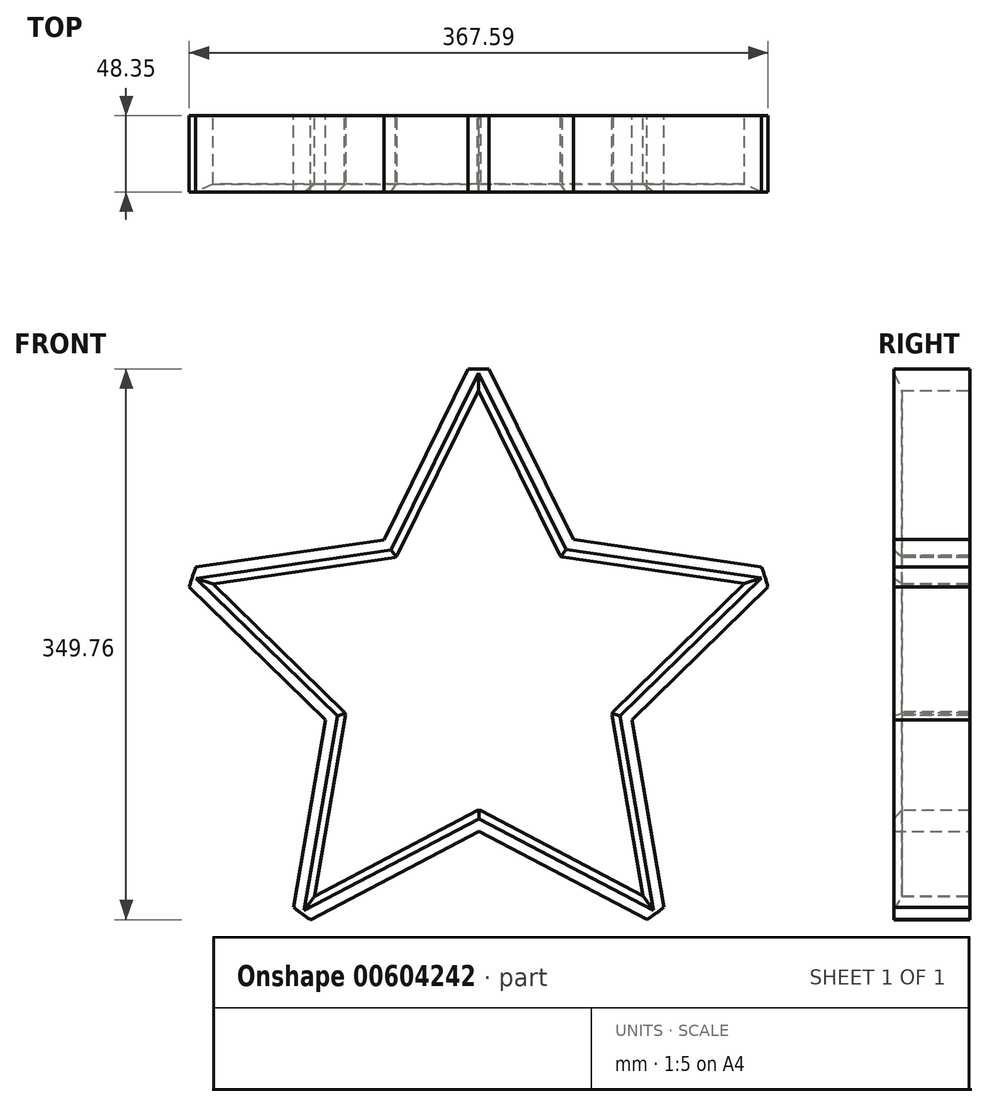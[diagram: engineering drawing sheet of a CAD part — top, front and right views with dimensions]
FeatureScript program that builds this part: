
annotation { "Feature Type Name" : "Feature", "Feature Type Description" : "" }
export const myFeature = defineFeature(function(context is Context, id is Id, definition is map)
    precondition{}
    {
        {
            var Q0;
            Q0=qCreatedBy(makeId("Front.planeOp"),FACE);
            var sketch = newSketch(context, id + "F0", { "sketchPlane" : qUnion([Q0])});
            skCircle(sketch, "E0", {"center": v(0, 0) * mm, "radius": 191.2 * mm});
            skCircle(sketch, "E1.cCircle", {"center": v(0, 0) * mm, "radius": 191.2 * mm, "construction": true});
            skLineSegment(sketch, "E2.0", {"start": v(0, -95.6) * mm, "end": v(-90.92, -29.54) * mm});
            skLineSegment(sketch, "E2.1", {"start": v(-90.92, -29.54) * mm, "end": v(-56.2, 77.34) * mm});
            skLineSegment(sketch, "E2.2", {"start": v(-56.2, 77.34) * mm, "end": v(56.2, 77.34) * mm});
            skLineSegment(sketch, "E2.3", {"start": v(56.2, 77.34) * mm, "end": v(90.92, -29.54) * mm});
            skLineSegment(sketch, "E2.4", {"start": v(90.92, -29.54) * mm, "end": v(0, -95.6) * mm});
            skLineSegment(sketch, "E3", {"start": v(-181.84, 59.08) * mm, "end": v(-90.92, -29.54) * mm});
            skLineSegment(sketch, "E4", {"start": v(-90.92, -29.54) * mm, "end": v(-112.38, -154.68) * mm});
            skLineSegment(sketch, "E5", {"start": v(-112.38, -154.68) * mm, "end": v(0, -95.6) * mm});
            skLineSegment(sketch, "E6", {"start": v(0, -95.6) * mm, "end": v(112.38, -154.68) * mm});
            skLineSegment(sketch, "E7", {"start": v(112.38, -154.68) * mm, "end": v(90.92, -29.54) * mm});
            skLineSegment(sketch, "E8", {"start": v(90.92, -29.54) * mm, "end": v(181.84, 59.08) * mm});
            skLineSegment(sketch, "E9", {"start": v(181.84, 59.08) * mm, "end": v(56.2, 77.34) * mm});
            skLineSegment(sketch, "E10", {"start": v(56.2, 77.34) * mm, "end": v(0, 191.2) * mm});
            skLineSegment(sketch, "E11", {"start": v(0, 191.2) * mm, "end": v(-56.2, 77.34) * mm});
            skLineSegment(sketch, "E12", {"start": v(-56.2, 77.34) * mm, "end": v(-181.84, 59.08) * mm});
            skLineSegment(sketch, "E13", {"start": v(-183.81, 52.63) * mm, "end": v(-92.15, -36.72) * mm});
            skLineSegment(sketch, "E14", {"start": v(-179.68, 65.36) * mm, "end": v(-88.85, -23.18) * mm});
            skLineSegment(sketch, "E15", {"start": v(-183.81, 52.63) * mm, "end": v(-58.3, 70.87) * mm});
            skLineSegment(sketch, "E16", {"start": v(-179.68, 65.36) * mm, "end": v(-53.02, 83.76) * mm});
            skLineSegment(sketch, "E17.2.0", {"start": v(6.63, 191.08) * mm, "end": v(63.28, 76.31) * mm});
            skLineSegment(sketch, "E17.2.1", {"start": v(-6.75, 191.08) * mm, "end": v(49.38, 77.34) * mm});
            skLineSegment(sketch, "E17.2.2", {"start": v(6.63, 191.08) * mm, "end": v(-49.5, 77.34) * mm});
            skLineSegment(sketch, "E17.2.3", {"start": v(-6.75, 191.08) * mm, "end": v(-63.4, 76.3) * mm});
            skLineSegment(sketch, "E17.4.0", {"start": v(183.78, 52.74) * mm, "end": v(92.13, -36.6) * mm});
            skLineSegment(sketch, "E17.4.1", {"start": v(179.64, 65.47) * mm, "end": v(88.82, -23.07) * mm});
            skLineSegment(sketch, "E17.4.2", {"start": v(183.78, 52.74) * mm, "end": v(58.26, 70.98) * mm});
            skLineSegment(sketch, "E17.4.3", {"start": v(179.64, 65.47) * mm, "end": v(52.97, 83.87) * mm});
            skLineSegment(sketch, "E17.anchor1", {"start": v(0, 0) * mm, "end": v(-179.68, 65.36) * mm, "construction": true});
            skLineSegment(sketch, "E17.anchor2", {"start": v(0, 0) * mm, "end": v(183.78, 52.74) * mm, "construction": true});
            skLineSegment(sketch, "E18.1.0", {"start": v(117.78, -150.62) * mm, "end": v(96.14, -24.46) * mm});
            skLineSegment(sketch, "E18.1.1", {"start": v(106.95, -158.5) * mm, "end": v(85.5, -33.47) * mm});
            skLineSegment(sketch, "E18.1.2", {"start": v(117.78, -150.62) * mm, "end": v(5.5, -91.6) * mm});
            skLineSegment(sketch, "E18.1.3", {"start": v(106.95, -158.5) * mm, "end": v(-6.34, -98.93) * mm});
            skLineSegment(sketch, "E18.2.0", {"start": v(-106.85, -158.56) * mm, "end": v(6.45, -98.99) * mm});
            skLineSegment(sketch, "E18.2.1", {"start": v(-117.68, -150.7) * mm, "end": v(-5.41, -91.67) * mm});
            skLineSegment(sketch, "E18.2.2", {"start": v(-106.85, -158.56) * mm, "end": v(-85.41, -33.54) * mm});
            skLineSegment(sketch, "E18.2.3", {"start": v(-117.68, -150.7) * mm, "end": v(-96.05, -24.54) * mm});
            skLineSegment(sketch, "E18.anchor1", {"start": v(0, 0) * mm, "end": v(52.97, 83.87) * mm, "construction": true});
            skLineSegment(sketch, "E18.anchor2", {"start": v(0, 0) * mm, "end": v(6.45, -98.99) * mm, "construction": true});
            skLineSegment(sketch, "E19", {"start": v(-58.3, 70.87) * mm, "end": v(-52.12, 71.76) * mm});
            skLineSegment(sketch, "E20", {"start": v(-49.5, 77.34) * mm, "end": v(-52.26, 71.74) * mm});
            skLineSegment(sketch, "E21.1.0", {"start": v(58.26, 70.98) * mm, "end": v(52.08, 71.88) * mm});
            skLineSegment(sketch, "E21.1.1", {"start": v(49.38, 77.34) * mm, "end": v(52.15, 71.75) * mm});
            skLineSegment(sketch, "E21.2.0", {"start": v(85.5, -33.47) * mm, "end": v(84.45, -27.32) * mm});
            skLineSegment(sketch, "E21.2.1", {"start": v(88.82, -23.07) * mm, "end": v(84.35, -27.42) * mm});
            skLineSegment(sketch, "E21.3.0", {"start": v(-5.41, -91.67) * mm, "end": v(0.11, -88.76) * mm});
            skLineSegment(sketch, "E21.3.1", {"start": v(5.5, -91.6) * mm, "end": v(-0.01, -88.7) * mm});
            skLineSegment(sketch, "E21.4.0", {"start": v(-88.85, -23.18) * mm, "end": v(-84.38, -27.54) * mm});
            skLineSegment(sketch, "E21.4.1", {"start": v(-85.41, -33.54) * mm, "end": v(-84.36, -27.4) * mm});
            skLineSegment(sketch, "E21.anchor1", {"start": v(0, 0) * mm, "end": v(-52.26, 71.74) * mm, "construction": true});
            skLineSegment(sketch, "E21.anchor2", {"start": v(0, 0) * mm, "end": v(-84.38, -27.54) * mm, "construction": true});
            skSolve(sketch);
        }
        {
            var Q0;
            {var subQ0=sQuery(id+"F0.wireOp",EDGE,"E11");var subQ5=sQuery(id+"F0.wireOp",EDGE,"E17.2.1");var subQ6=makeQuery(id+"F0.imprint","INTERSECT",VERTEX,{"derivedFrom":[subQ0,subQ5]});Q0=makeQuery(id+"F0.imprint","IMPRINT",FACE,{"disambiguationData":[TD([[makeQuery(id+"F0.imprint","IMPRINT",EDGE,{"disambiguationData":[TD([[subQ6,-1.0]])],"derivedFrom":subQ5}),1.0]])]});}
            var Q1;
            {var subQ0=sQuery(id+"F0.wireOp",EDGE,"E10");var subQ3=sQuery(id+"F0.wireOp",EDGE,"E17.2.2");var subQ5=makeQuery(id+"F0.imprint","INTERSECT",VERTEX,{"derivedFrom":[subQ0,subQ3]});Q1=makeQuery(id+"F0.imprint","IMPRINT",FACE,{"disambiguationData":[TD([[makeQuery(id+"F0.imprint","IMPRINT",EDGE,{"disambiguationData":[TD([[subQ5,-1.0]])],"derivedFrom":subQ0}),-1.0]])]});}
            var Q2;
            {var subQ0=sQuery(id+"F0.wireOp",EDGE,"E11");var subQ3=sQuery(id+"F0.wireOp",EDGE,"E17.2.1");var subQ5=makeQuery(id+"F0.imprint","INTERSECT",VERTEX,{"derivedFrom":[subQ0,subQ3]});Q2=makeQuery(id+"F0.imprint","IMPRINT",FACE,{"disambiguationData":[TD([[makeQuery(id+"F0.imprint","IMPRINT",EDGE,{"disambiguationData":[TD([[subQ5,1.0]])],"derivedFrom":subQ0}),-1.0]])]});}
            var Q3;
            {var subQ0=sQuery(id+"F0.wireOp",EDGE,"E16");var subQ1=sQuery(id+"F0.wireOp",EDGE,"E11");var subQ2=makeQuery(id+"F0.imprint","INTERSECT",VERTEX,{"derivedFrom":[subQ1,subQ0]});Q3=makeQuery(id+"F0.imprint","IMPRINT",FACE,{"disambiguationData":[TD([[makeQuery(id+"F0.imprint","IMPRINT",EDGE,{"disambiguationData":[TD([[subQ2,1.0]])],"derivedFrom":subQ1}),-1.0]])]});}
            var Q4;
            {var subQ1=sQuery(id+"F0.wireOp",EDGE,"E11");var subQ5=makeQuery(id+"F0.imprint","INTERSECT",VERTEX,{"derivedFrom":[subQ1,sQuery(id+"F0.wireOp",EDGE,"E16")]});Q4=makeQuery(id+"F0.imprint","IMPRINT",FACE,{"disambiguationData":[TD([[makeQuery(id+"F0.imprint","IMPRINT",EDGE,{"disambiguationData":[TD([[subQ5,1.0]])],"derivedFrom":subQ1}),1.0]])]});}
            var Q5;
            {var subQ5=sQuery(id+"F0.wireOp",EDGE,"E10");var subQ6=makeQuery(id+"F0.imprint","INTERSECT",VERTEX,{"derivedFrom":[subQ5,sQuery(id+"F0.wireOp",EDGE,"E17.4.3")]});Q5=makeQuery(id+"F0.imprint","IMPRINT",FACE,{"disambiguationData":[TD([[makeQuery(id+"F0.imprint","IMPRINT",EDGE,{"disambiguationData":[TD([[subQ6,-1.0]])],"derivedFrom":subQ5}),1.0]])]});}
            var Q6;
            {var subQ0=sQuery(id+"F0.wireOp",EDGE,"E17.4.3");var subQ1=sQuery(id+"F0.wireOp",EDGE,"E10");var subQ2=makeQuery(id+"F0.imprint","INTERSECT",VERTEX,{"derivedFrom":[subQ1,subQ0]});Q6=makeQuery(id+"F0.imprint","IMPRINT",FACE,{"disambiguationData":[TD([[makeQuery(id+"F0.imprint","IMPRINT",EDGE,{"disambiguationData":[TD([[subQ2,-1.0]])],"derivedFrom":subQ1}),-1.0]])]});}
            var Q7;
            {var subQ5=sQuery(id+"F0.wireOp",EDGE,"E21.1.0");Q7=makeQuery(id+"F0.imprint","IMPRINT",FACE,{"disambiguationData":[TD([[makeQuery(id+"F0.imprint","IMPRINT",EDGE,{"derivedFrom":subQ5}),-1.0]])]});}
            var Q8;
            {var subQ1=sQuery(id+"F0.wireOp",EDGE,"E9");var subQ3=sQuery(id+"F0.wireOp",EDGE,"E17.2.0");var subQ4=makeQuery(id+"F0.imprint","INTERSECT",VERTEX,{"derivedFrom":[subQ1,subQ3]});Q8=makeQuery(id+"F0.imprint","IMPRINT",FACE,{"disambiguationData":[TD([[makeQuery(id+"F0.imprint","IMPRINT",EDGE,{"disambiguationData":[TD([[subQ4,1.0]])],"derivedFrom":subQ3}),-1.0]])]});}
            var Q9;
            {var subQ0=sQuery(id+"F0.wireOp",EDGE,"E17.2.0");var subQ1=sQuery(id+"F0.wireOp",EDGE,"E9");var subQ2=makeQuery(id+"F0.imprint","INTERSECT",VERTEX,{"derivedFrom":[subQ1,subQ0]});Q9=makeQuery(id+"F0.imprint","IMPRINT",FACE,{"disambiguationData":[TD([[makeQuery(id+"F0.imprint","IMPRINT",EDGE,{"disambiguationData":[TD([[subQ2,1.0]])],"derivedFrom":subQ1}),-1.0]])]});}
            var Q10;
            {var subQ1=sQuery(id+"F0.wireOp",EDGE,"E9");var subQ7=makeQuery(id+"F0.imprint","INTERSECT",VERTEX,{"derivedFrom":[subQ1,sQuery(id+"F0.wireOp",EDGE,"E17.2.0")]});Q10=makeQuery(id+"F0.imprint","IMPRINT",FACE,{"disambiguationData":[TD([[makeQuery(id+"F0.imprint","IMPRINT",EDGE,{"disambiguationData":[TD([[subQ7,1.0]])],"derivedFrom":subQ1}),1.0]])]});}
            var Q11;
            {var subQ5=sQuery(id+"F0.wireOp",EDGE,"E8");var subQ7=makeQuery(id+"F0.imprint","INTERSECT",VERTEX,{"derivedFrom":[subQ5,sQuery(id+"F0.wireOp",EDGE,"E18.1.0")]});Q11=makeQuery(id+"F0.imprint","IMPRINT",FACE,{"disambiguationData":[TD([[makeQuery(id+"F0.imprint","IMPRINT",EDGE,{"disambiguationData":[TD([[subQ7,-1.0]])],"derivedFrom":subQ5}),1.0]])]});}
            var Q12;
            {var subQ0=sQuery(id+"F0.wireOp",EDGE,"E18.1.0");var subQ1=sQuery(id+"F0.wireOp",EDGE,"E8");var subQ2=makeQuery(id+"F0.imprint","INTERSECT",VERTEX,{"derivedFrom":[subQ1,subQ0]});Q12=makeQuery(id+"F0.imprint","IMPRINT",FACE,{"disambiguationData":[TD([[makeQuery(id+"F0.imprint","IMPRINT",EDGE,{"disambiguationData":[TD([[subQ2,-1.0]])],"derivedFrom":subQ1}),-1.0]])]});}
            var Q13;
            {var subQ0=sQuery(id+"F0.wireOp",EDGE,"E9");var subQ5=sQuery(id+"F0.wireOp",EDGE,"E17.4.1");var subQ6=makeQuery(id+"F0.imprint","INTERSECT",VERTEX,{"derivedFrom":[subQ0,subQ5]});Q13=makeQuery(id+"F0.imprint","IMPRINT",FACE,{"disambiguationData":[TD([[makeQuery(id+"F0.imprint","IMPRINT",EDGE,{"disambiguationData":[TD([[subQ6,-1.0]])],"derivedFrom":subQ5}),1.0]])]});}
            var Q14;
            {var subQ0=sQuery(id+"F0.wireOp",EDGE,"E9");var subQ3=sQuery(id+"F0.wireOp",EDGE,"E17.4.1");var subQ5=makeQuery(id+"F0.imprint","INTERSECT",VERTEX,{"derivedFrom":[subQ0,subQ3]});Q14=makeQuery(id+"F0.imprint","IMPRINT",FACE,{"disambiguationData":[TD([[makeQuery(id+"F0.imprint","IMPRINT",EDGE,{"disambiguationData":[TD([[subQ5,1.0]])],"derivedFrom":subQ0}),-1.0]])]});}
            var Q15;
            {var subQ0=sQuery(id+"F0.wireOp",EDGE,"E8");var subQ3=sQuery(id+"F0.wireOp",EDGE,"E17.4.2");var subQ5=makeQuery(id+"F0.imprint","INTERSECT",VERTEX,{"derivedFrom":[subQ0,subQ3]});Q15=makeQuery(id+"F0.imprint","IMPRINT",FACE,{"disambiguationData":[TD([[makeQuery(id+"F0.imprint","IMPRINT",EDGE,{"disambiguationData":[TD([[subQ5,-1.0]])],"derivedFrom":subQ0}),-1.0]])]});}
            var Q16;
            {var subQ5=sQuery(id+"F0.wireOp",EDGE,"E21.2.0");Q16=makeQuery(id+"F0.imprint","IMPRINT",FACE,{"disambiguationData":[TD([[makeQuery(id+"F0.imprint","IMPRINT",EDGE,{"derivedFrom":subQ5}),-1.0]])]});}
            var Q17;
            {var subQ1=sQuery(id+"F0.wireOp",EDGE,"E7");var subQ3=sQuery(id+"F0.wireOp",EDGE,"E17.4.0");var subQ4=makeQuery(id+"F0.imprint","INTERSECT",VERTEX,{"derivedFrom":[subQ1,subQ3]});Q17=makeQuery(id+"F0.imprint","IMPRINT",FACE,{"disambiguationData":[TD([[makeQuery(id+"F0.imprint","IMPRINT",EDGE,{"disambiguationData":[TD([[subQ4,1.0]])],"derivedFrom":subQ3}),-1.0]])]});}
            var Q18;
            {var subQ5=sQuery(id+"F0.wireOp",EDGE,"E7");var subQ7=makeQuery(id+"F0.imprint","INTERSECT",VERTEX,{"derivedFrom":[subQ5,sQuery(id+"F0.wireOp",EDGE,"E17.4.0")]});Q18=makeQuery(id+"F0.imprint","IMPRINT",FACE,{"disambiguationData":[TD([[makeQuery(id+"F0.imprint","IMPRINT",EDGE,{"disambiguationData":[TD([[subQ7,1.0]])],"derivedFrom":subQ5}),1.0]])]});}
            var Q19;
            {var subQ0=sQuery(id+"F0.wireOp",EDGE,"E17.4.0");var subQ1=sQuery(id+"F0.wireOp",EDGE,"E7");var subQ2=makeQuery(id+"F0.imprint","INTERSECT",VERTEX,{"derivedFrom":[subQ1,subQ0]});Q19=makeQuery(id+"F0.imprint","IMPRINT",FACE,{"disambiguationData":[TD([[makeQuery(id+"F0.imprint","IMPRINT",EDGE,{"disambiguationData":[TD([[subQ2,1.0]])],"derivedFrom":subQ1}),-1.0]])]});}
            var Q20;
            {var subQ1=sQuery(id+"F0.wireOp",EDGE,"E6");var subQ3=sQuery(id+"F0.wireOp",EDGE,"E18.1.1");var subQ4=makeQuery(id+"F0.imprint","INTERSECT",VERTEX,{"derivedFrom":[subQ1,subQ3]});Q20=makeQuery(id+"F0.imprint","IMPRINT",FACE,{"disambiguationData":[TD([[makeQuery(id+"F0.imprint","IMPRINT",EDGE,{"disambiguationData":[TD([[subQ4,-1.0]])],"derivedFrom":subQ3}),-1.0]])]});}
            var Q21;
            {var subQ0=sQuery(id+"F0.wireOp",EDGE,"E7");var subQ3=sQuery(id+"F0.wireOp",EDGE,"E18.1.2");var subQ5=makeQuery(id+"F0.imprint","INTERSECT",VERTEX,{"derivedFrom":[subQ0,subQ3]});Q21=makeQuery(id+"F0.imprint","IMPRINT",FACE,{"disambiguationData":[TD([[makeQuery(id+"F0.imprint","IMPRINT",EDGE,{"disambiguationData":[TD([[subQ5,1.0]])],"derivedFrom":subQ0}),-1.0]])]});}
            var Q22;
            {var subQ0=sQuery(id+"F0.wireOp",EDGE,"E6");var subQ3=sQuery(id+"F0.wireOp",EDGE,"E18.1.1");var subQ5=makeQuery(id+"F0.imprint","INTERSECT",VERTEX,{"derivedFrom":[subQ0,subQ3]});Q22=makeQuery(id+"F0.imprint","IMPRINT",FACE,{"disambiguationData":[TD([[makeQuery(id+"F0.imprint","IMPRINT",EDGE,{"disambiguationData":[TD([[subQ5,-1.0]])],"derivedFrom":subQ0}),-1.0]])]});}
            var Q23;
            {var subQ0=sQuery(id+"F0.wireOp",EDGE,"E18.2.0");var subQ1=sQuery(id+"F0.wireOp",EDGE,"E6");var subQ2=makeQuery(id+"F0.imprint","INTERSECT",VERTEX,{"derivedFrom":[subQ1,subQ0]});Q23=makeQuery(id+"F0.imprint","IMPRINT",FACE,{"disambiguationData":[TD([[makeQuery(id+"F0.imprint","IMPRINT",EDGE,{"disambiguationData":[TD([[subQ2,-1.0]])],"derivedFrom":subQ1}),-1.0]])]});}
            var Q24;
            {var subQ1=sQuery(id+"F0.wireOp",EDGE,"E6");var subQ5=makeQuery(id+"F0.imprint","INTERSECT",VERTEX,{"derivedFrom":[subQ1,sQuery(id+"F0.wireOp",EDGE,"E18.2.0")]});Q24=makeQuery(id+"F0.imprint","IMPRINT",FACE,{"disambiguationData":[TD([[makeQuery(id+"F0.imprint","IMPRINT",EDGE,{"disambiguationData":[TD([[subQ5,-1.0]])],"derivedFrom":subQ1}),1.0]])]});}
            var Q25;
            {var subQ1=sQuery(id+"F0.wireOp",EDGE,"E5");var subQ3=sQuery(id+"F0.wireOp",EDGE,"E18.1.3");var subQ4=makeQuery(id+"F0.imprint","INTERSECT",VERTEX,{"derivedFrom":[subQ1,subQ3]});Q25=makeQuery(id+"F0.imprint","IMPRINT",FACE,{"disambiguationData":[TD([[makeQuery(id+"F0.imprint","IMPRINT",EDGE,{"disambiguationData":[TD([[subQ4,1.0]])],"derivedFrom":subQ3}),-1.0]])]});}
            var Q26;
            {var subQ3=sQuery(id+"F0.wireOp",EDGE,"E21.3.0");Q26=makeQuery(id+"F0.imprint","IMPRINT",FACE,{"disambiguationData":[TD([[makeQuery(id+"F0.imprint","IMPRINT",EDGE,{"derivedFrom":subQ3}),-1.0]])]});}
            var Q27;
            {var subQ5=sQuery(id+"F0.wireOp",EDGE,"E5");var subQ7=makeQuery(id+"F0.imprint","INTERSECT",VERTEX,{"derivedFrom":[subQ5,sQuery(id+"F0.wireOp",EDGE,"E18.1.3")]});Q27=makeQuery(id+"F0.imprint","IMPRINT",FACE,{"disambiguationData":[TD([[makeQuery(id+"F0.imprint","IMPRINT",EDGE,{"disambiguationData":[TD([[subQ7,1.0]])],"derivedFrom":subQ5}),1.0]])]});}
            var Q28;
            {var subQ0=sQuery(id+"F0.wireOp",EDGE,"E18.1.3");var subQ1=sQuery(id+"F0.wireOp",EDGE,"E5");var subQ2=makeQuery(id+"F0.imprint","INTERSECT",VERTEX,{"derivedFrom":[subQ1,subQ0]});Q28=makeQuery(id+"F0.imprint","IMPRINT",FACE,{"disambiguationData":[TD([[makeQuery(id+"F0.imprint","IMPRINT",EDGE,{"disambiguationData":[TD([[subQ2,1.0]])],"derivedFrom":subQ1}),-1.0]])]});}
            var Q29;
            {var subQ1=sQuery(id+"F0.wireOp",EDGE,"E4");var subQ3=sQuery(id+"F0.wireOp",EDGE,"E18.2.1");var subQ4=makeQuery(id+"F0.imprint","INTERSECT",VERTEX,{"derivedFrom":[subQ1,subQ3]});Q29=makeQuery(id+"F0.imprint","IMPRINT",FACE,{"disambiguationData":[TD([[makeQuery(id+"F0.imprint","IMPRINT",EDGE,{"disambiguationData":[TD([[subQ4,-1.0]])],"derivedFrom":subQ3}),-1.0]])]});}
            var Q30;
            {var subQ0=sQuery(id+"F0.wireOp",EDGE,"E4");var subQ3=sQuery(id+"F0.wireOp",EDGE,"E18.2.1");var subQ5=makeQuery(id+"F0.imprint","INTERSECT",VERTEX,{"derivedFrom":[subQ0,subQ3]});Q30=makeQuery(id+"F0.imprint","IMPRINT",FACE,{"disambiguationData":[TD([[makeQuery(id+"F0.imprint","IMPRINT",EDGE,{"disambiguationData":[TD([[subQ5,-1.0]])],"derivedFrom":subQ0}),-1.0]])]});}
            var Q31;
            {var subQ0=sQuery(id+"F0.wireOp",EDGE,"E5");var subQ3=sQuery(id+"F0.wireOp",EDGE,"E18.2.2");var subQ5=makeQuery(id+"F0.imprint","INTERSECT",VERTEX,{"derivedFrom":[subQ0,subQ3]});Q31=makeQuery(id+"F0.imprint","IMPRINT",FACE,{"disambiguationData":[TD([[makeQuery(id+"F0.imprint","IMPRINT",EDGE,{"disambiguationData":[TD([[subQ5,1.0]])],"derivedFrom":subQ0}),-1.0]])]});}
            var Q32;
            {var subQ0=sQuery(id+"F0.wireOp",EDGE,"E4");var subQ1=makeQuery(id+"F0.imprint","INTERSECT",VERTEX,{"derivedFrom":[subQ0,sQuery(id+"F0.wireOp",EDGE,"E13")]});Q32=makeQuery(id+"F0.imprint","IMPRINT",FACE,{"disambiguationData":[TD([[makeQuery(id+"F0.imprint","IMPRINT",EDGE,{"disambiguationData":[TD([[subQ1,-1.0]])],"derivedFrom":subQ0}),1.0]])]});}
            var Q33;
            {var subQ0=sQuery(id+"F0.wireOp",EDGE,"E13");var subQ1=sQuery(id+"F0.wireOp",EDGE,"E4");var subQ2=makeQuery(id+"F0.imprint","INTERSECT",VERTEX,{"derivedFrom":[subQ1,subQ0]});Q33=makeQuery(id+"F0.imprint","IMPRINT",FACE,{"disambiguationData":[TD([[makeQuery(id+"F0.imprint","IMPRINT",EDGE,{"disambiguationData":[TD([[subQ2,-1.0]])],"derivedFrom":subQ1}),-1.0]])]});}
            var Q34;
            {var subQ5=sQuery(id+"F0.wireOp",EDGE,"E21.4.0");Q34=makeQuery(id+"F0.imprint","IMPRINT",FACE,{"disambiguationData":[TD([[makeQuery(id+"F0.imprint","IMPRINT",EDGE,{"derivedFrom":subQ5}),-1.0]])]});}
            var Q35;
            {var subQ0=sQuery(id+"F0.wireOp",EDGE,"E4");var subQ5=sQuery(id+"F0.wireOp",EDGE,"E13");var subQ6=makeQuery(id+"F0.imprint","INTERSECT",VERTEX,{"derivedFrom":[subQ0,subQ5]});Q35=makeQuery(id+"F0.imprint","IMPRINT",FACE,{"disambiguationData":[TD([[makeQuery(id+"F0.imprint","IMPRINT",EDGE,{"disambiguationData":[TD([[subQ6,1.0]])],"derivedFrom":subQ5}),1.0]])]});}
            var Q36;
            {var subQ5=sQuery(id+"F0.wireOp",EDGE,"E3");var subQ6=makeQuery(id+"F0.imprint","INTERSECT",VERTEX,{"derivedFrom":[subQ5,sQuery(id+"F0.wireOp",EDGE,"E18.2.3")]});Q36=makeQuery(id+"F0.imprint","IMPRINT",FACE,{"disambiguationData":[TD([[makeQuery(id+"F0.imprint","IMPRINT",EDGE,{"disambiguationData":[TD([[subQ6,1.0]])],"derivedFrom":subQ5}),1.0]])]});}
            var Q37;
            {var subQ0=sQuery(id+"F0.wireOp",EDGE,"E18.2.3");var subQ1=sQuery(id+"F0.wireOp",EDGE,"E3");var subQ2=makeQuery(id+"F0.imprint","INTERSECT",VERTEX,{"derivedFrom":[subQ1,subQ0]});Q37=makeQuery(id+"F0.imprint","IMPRINT",FACE,{"disambiguationData":[TD([[makeQuery(id+"F0.imprint","IMPRINT",EDGE,{"disambiguationData":[TD([[subQ2,1.0]])],"derivedFrom":subQ1}),-1.0]])]});}
            var Q38;
            {var subQ0=sQuery(id+"F0.wireOp",EDGE,"E12");var subQ5=sQuery(id+"F0.wireOp",EDGE,"E14");var subQ6=makeQuery(id+"F0.imprint","INTERSECT",VERTEX,{"derivedFrom":[subQ0,subQ5]});Q38=makeQuery(id+"F0.imprint","IMPRINT",FACE,{"disambiguationData":[TD([[makeQuery(id+"F0.imprint","IMPRINT",EDGE,{"disambiguationData":[TD([[subQ6,-1.0]])],"derivedFrom":subQ5}),-1.0]])]});}
            var Q39;
            {var subQ0=sQuery(id+"F0.wireOp",EDGE,"E3");var subQ3=sQuery(id+"F0.wireOp",EDGE,"E15");var subQ5=makeQuery(id+"F0.imprint","INTERSECT",VERTEX,{"derivedFrom":[subQ0,subQ3]});Q39=makeQuery(id+"F0.imprint","IMPRINT",FACE,{"disambiguationData":[TD([[makeQuery(id+"F0.imprint","IMPRINT",EDGE,{"disambiguationData":[TD([[subQ5,1.0]])],"derivedFrom":subQ0}),-1.0]])]});}
            var Q40;
            {var subQ0=sQuery(id+"F0.wireOp",EDGE,"E12");var subQ3=sQuery(id+"F0.wireOp",EDGE,"E14");var subQ5=makeQuery(id+"F0.imprint","INTERSECT",VERTEX,{"derivedFrom":[subQ0,subQ3]});Q40=makeQuery(id+"F0.imprint","IMPRINT",FACE,{"disambiguationData":[TD([[makeQuery(id+"F0.imprint","IMPRINT",EDGE,{"disambiguationData":[TD([[subQ5,-1.0]])],"derivedFrom":subQ0}),-1.0]])]});}
            var Q41;
            {var subQ0=sQuery(id+"F0.wireOp",EDGE,"E17.2.3");var subQ1=sQuery(id+"F0.wireOp",EDGE,"E12");var subQ2=makeQuery(id+"F0.imprint","INTERSECT",VERTEX,{"derivedFrom":[subQ1,subQ0]});Q41=makeQuery(id+"F0.imprint","IMPRINT",FACE,{"disambiguationData":[TD([[makeQuery(id+"F0.imprint","IMPRINT",EDGE,{"disambiguationData":[TD([[subQ2,-1.0]])],"derivedFrom":subQ1}),-1.0]])]});}
            var Q42;
            {var subQ1=sQuery(id+"F0.wireOp",EDGE,"E12");var subQ5=makeQuery(id+"F0.imprint","INTERSECT",VERTEX,{"derivedFrom":[subQ1,sQuery(id+"F0.wireOp",EDGE,"E17.2.3")]});Q42=makeQuery(id+"F0.imprint","IMPRINT",FACE,{"disambiguationData":[TD([[makeQuery(id+"F0.imprint","IMPRINT",EDGE,{"disambiguationData":[TD([[subQ5,-1.0]])],"derivedFrom":subQ1}),1.0]])]});}
            var Q43;
            {var subQ1=sQuery(id+"F0.wireOp",EDGE,"E11");var subQ3=sQuery(id+"F0.wireOp",EDGE,"E16");var subQ4=makeQuery(id+"F0.imprint","INTERSECT",VERTEX,{"derivedFrom":[subQ1,subQ3]});Q43=makeQuery(id+"F0.imprint","IMPRINT",FACE,{"disambiguationData":[TD([[makeQuery(id+"F0.imprint","IMPRINT",EDGE,{"disambiguationData":[TD([[subQ4,1.0]])],"derivedFrom":subQ3}),-1.0]])]});}
            var Q44;
            {var subQ5=sQuery(id+"F0.wireOp",EDGE,"E20");Q44=makeQuery(id+"F0.imprint","IMPRINT",FACE,{"disambiguationData":[TD([[makeQuery(id+"F0.imprint","IMPRINT",EDGE,{"derivedFrom":subQ5}),-1.0]])]});}
            extrude(context, id + "F1", {"entities" : qUnion([Q0, Q1, Q2, Q3, Q4, Q5, Q6, Q7, Q8, Q9, Q10, Q11, Q12, Q13, Q14, Q15, Q16, Q17, Q18, Q19, Q20, Q21, Q22, Q23, Q24, Q25, Q26, Q27, Q28, Q29, Q30, Q31, Q32, Q33, Q34, Q35, Q36, Q37, Q38, Q39, Q40, Q41, Q42, Q43, Q44]), "depth" : 48.35 * mm, "offsetDistance" : 25 * mm});
        }
        {
            var Q0;
            Q0=makeQuery(id+"F1.opExtrude","CAP_EDGE",EDGE,{"disambiguationData":[OSD([sQuery(id+"F0.wireOp",EDGE,"E14"),sQuery(id+"F0.wireOp",EDGE,"E21.4.0")])],"isStart":false});
            var Q1;
            Q1=makeQuery(id+"F1.opExtrude","CAP_EDGE",EDGE,{"disambiguationData":[OSD([sQuery(id+"F0.wireOp",EDGE,"E18.2.2"),sQuery(id+"F0.wireOp",EDGE,"E21.4.1")])],"isStart":false});
            var Q2;
            Q2=makeQuery(id+"F1.opExtrude","CAP_EDGE",EDGE,{"disambiguationData":[OSD([sQuery(id+"F0.wireOp",EDGE,"E18.2.1"),sQuery(id+"F0.wireOp",EDGE,"E21.3.0")])],"isStart":false});
            var Q3;
            Q3=makeQuery(id+"F1.opExtrude","CAP_EDGE",EDGE,{"disambiguationData":[OSD([sQuery(id+"F0.wireOp",EDGE,"E18.1.2"),sQuery(id+"F0.wireOp",EDGE,"E21.3.1")])],"isStart":false});
            var Q4;
            Q4=makeQuery(id+"F1.opExtrude","CAP_EDGE",EDGE,{"disambiguationData":[OSD([sQuery(id+"F0.wireOp",EDGE,"E18.1.1"),sQuery(id+"F0.wireOp",EDGE,"E21.2.0")])],"isStart":false});
            var Q5;
            Q5=makeQuery(id+"F1.opExtrude","CAP_EDGE",EDGE,{"disambiguationData":[OSD([sQuery(id+"F0.wireOp",EDGE,"E17.4.1"),sQuery(id+"F0.wireOp",EDGE,"E21.2.1")])],"isStart":false});
            var Q6;
            Q6=makeQuery(id+"F1.opExtrude","CAP_EDGE",EDGE,{"disambiguationData":[OSD([sQuery(id+"F0.wireOp",EDGE,"E17.4.2"),sQuery(id+"F0.wireOp",EDGE,"E21.1.0")])],"isStart":false});
            var Q7;
            Q7=makeQuery(id+"F1.opExtrude","CAP_EDGE",EDGE,{"disambiguationData":[OSD([sQuery(id+"F0.wireOp",EDGE,"E17.2.1"),sQuery(id+"F0.wireOp",EDGE,"E21.1.1")])],"isStart":false});
            var Q8;
            Q8=makeQuery(id+"F1.opExtrude","CAP_EDGE",EDGE,{"disambiguationData":[OSD([sQuery(id+"F0.wireOp",EDGE,"E17.2.2"),sQuery(id+"F0.wireOp",EDGE,"E20")])],"isStart":false});
            var Q9;
            Q9=makeQuery(id+"F1.opExtrude","CAP_EDGE",EDGE,{"disambiguationData":[OSD([sQuery(id+"F0.wireOp",EDGE,"E15"),sQuery(id+"F0.wireOp",EDGE,"E19")])],"isStart":false});
            chamfer(context, id + "F2", {"entities" : qUnion([Q0, Q1, Q2, Q3, Q4, Q5, Q6, Q7, Q8, Q9]), "width" : 5 * mm, "tangentPropagation" : true});
        }
        {
            var Q0;
            Q0=makeQuery(id+"F1.opExtrude","SWEPT_EDGE",EDGE,{"disambiguationData":[OSD([sQuery(id+"F0.wireOp",EDGE,"E21.4.0"),sQuery(id+"F0.wireOp",EDGE,"E21.4.1")])]});
            var Q1;
            Q1=makeQuery(id+"F1.opExtrude","SWEPT_EDGE",EDGE,{"disambiguationData":[OSD([sQuery(id+"F0.wireOp",EDGE,"E19"),sQuery(id+"F0.wireOp",EDGE,"E20")])]});
            var Q2;
            Q2=makeQuery(id+"F1.opExtrude","SWEPT_EDGE",EDGE,{"disambiguationData":[OSD([sQuery(id+"F0.wireOp",EDGE,"E21.3.0"),sQuery(id+"F0.wireOp",EDGE,"E21.3.1")])]});
            var Q3;
            Q3=makeQuery(id+"F1.opExtrude","SWEPT_EDGE",EDGE,{"disambiguationData":[OSD([sQuery(id+"F0.wireOp",EDGE,"E21.2.0"),sQuery(id+"F0.wireOp",EDGE,"E21.2.1")])]});
            var Q4;
            Q4=makeQuery(id+"F1.opExtrude","SWEPT_EDGE",EDGE,{"disambiguationData":[OSD([sQuery(id+"F0.wireOp",EDGE,"E21.1.0"),sQuery(id+"F0.wireOp",EDGE,"E21.1.1")])]});
            chamfer(context, id + "F3", {"entities" : qUnion([Q0, Q1, Q2, Q3, Q4]), "width" : 2 * mm, "tangentPropagation" : true});
        }
    });
